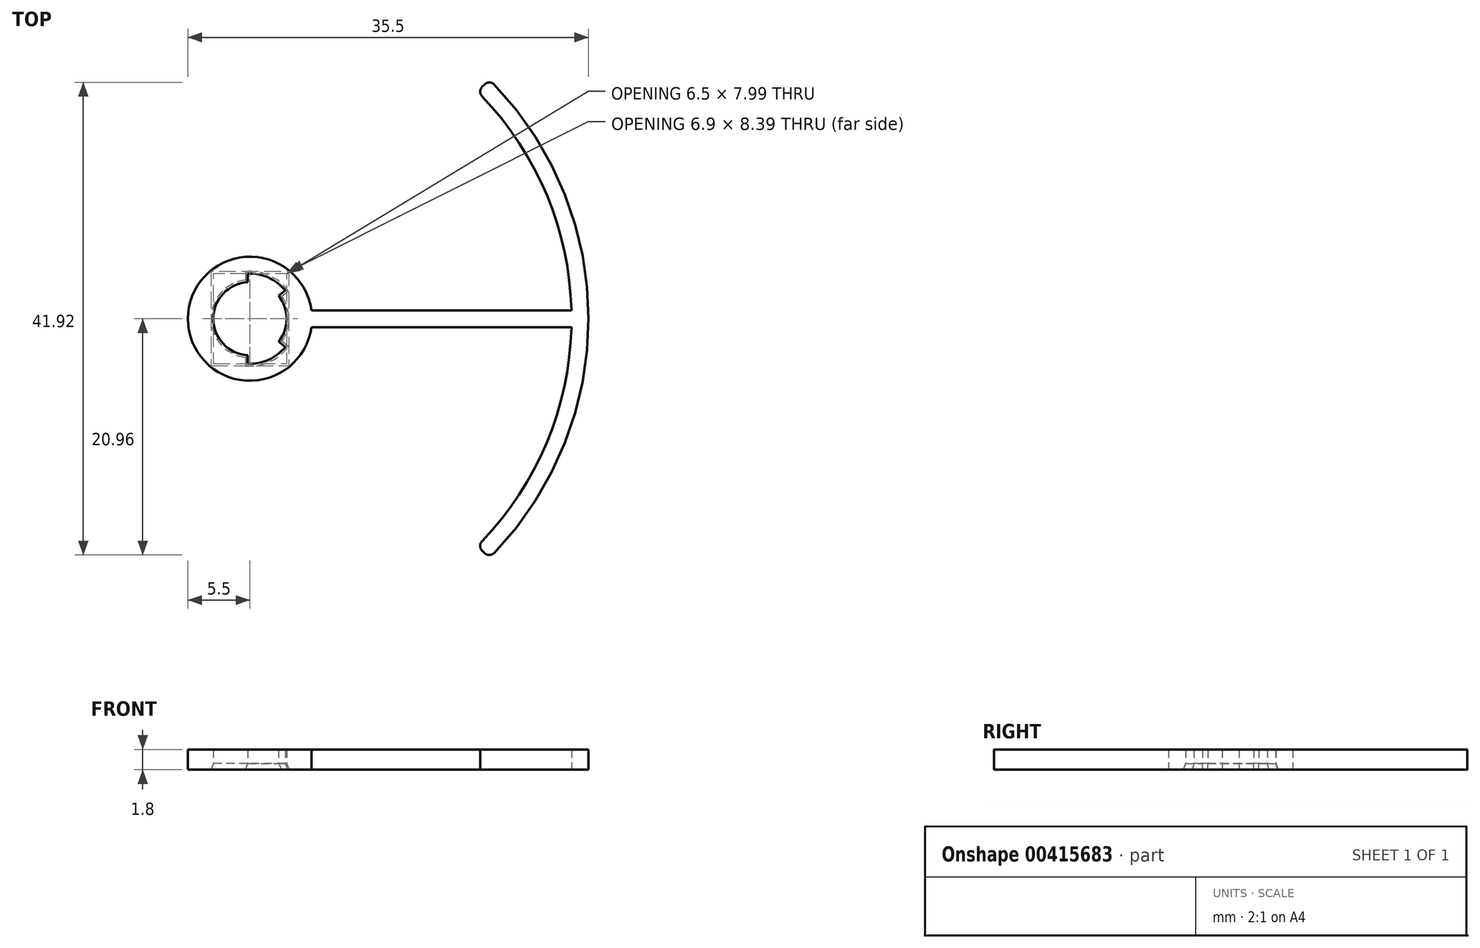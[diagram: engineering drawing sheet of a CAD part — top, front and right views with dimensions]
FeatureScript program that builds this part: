
annotation { "Feature Type Name" : "Feature", "Feature Type Description" : "" }
export const myFeature = defineFeature(function(context is Context, id is Id, definition is map)
    precondition{}
    {
        {
            var Q0;
            Q0=qCreatedBy(makeId("Top.planeOp"),FACE);
            var sketch = newSketch(context, id + "F0", { "sketchPlane" : qUnion([Q0])});
            skCircle(sketch, "E0", {"center": v(0, 0) * mm, "radius": 4 * mm});
            skCircle(sketch, "E1", {"center": v(0, 0) * mm, "radius": 3.25 * mm});
            skCircle(sketch, "E2", {"center": v(0, 0) * mm, "radius": 5.5 * mm});
            skLineSegment(sketch, "E3", {"start": v(-0.2, 4) * mm, "end": v(-0.2, -4) * mm});
            skLineSegment(sketch, "E4", {"start": v(0, 0) * mm, "end": v(3.12, -2.5) * mm});
            skLineSegment(sketch, "E5", {"start": v(0, 0) * mm, "end": v(3.12, 2.5) * mm});
            skPoint(sketch, "E6", {"position": v(3.12, 0) * mm});
            skLineSegment(sketch, "E7.bottom", {"start": v(5.45, -0.75) * mm, "end": v(30, -0.75) * mm});
            skLineSegment(sketch, "E7.top", {"start": v(5.45, 0.75) * mm, "end": v(30, 0.75) * mm});
            skLineSegment(sketch, "E7.left", {"start": v(5.45, -0.75) * mm, "end": v(5.45, 0.75) * mm});
            skLineSegment(sketch, "E7.right", {"start": v(30, -0.75) * mm, "end": v(30, 0.75) * mm});
            skPoint(sketch, "E7.middle", {"position": v(17.72, 0) * mm});
            skCircle(sketch, "E8", {"center": v(0, 0) * mm, "radius": 30 * mm});
            skCircle(sketch, "E9", {"center": v(0, 0) * mm, "radius": 28.5 * mm});
            skLineSegment(sketch, "E10", {"start": v(0, 0) * mm, "end": v(21.21, -21.21) * mm});
            skLineSegment(sketch, "E11", {"start": v(0, 0) * mm, "end": v(21.21, 21.21) * mm});
            skSolve(sketch);
        }
        {
            var Q0;
            {var subQ1=sQuery(id+"F0.wireOp",EDGE,"E7.right");Q0=makeQuery(id+"F0.imprint","IMPRINT",FACE,{"disambiguationData":[TD([[makeQuery(id+"F0.imprint","IMPRINT",EDGE,{"derivedFrom":subQ1}),1.0]])]});}
            var Q1;
            {var subQ1=sQuery(id+"F0.wireOp",EDGE,"E7.top");var subQ3=sQuery(id+"F0.wireOp",EDGE,"E9");var subQ4=makeQuery(id+"F0.imprint","INTERSECT",VERTEX,{"derivedFrom":[subQ1,subQ3]});Q1=makeQuery(id+"F0.imprint","IMPRINT",FACE,{"disambiguationData":[TD([[makeQuery(id+"F0.imprint","IMPRINT",EDGE,{"disambiguationData":[TD([[subQ4,-1.0]])],"derivedFrom":subQ3}),-1.0]])]});}
            var Q2;
            {var subQ1=sQuery(id+"F0.wireOp",EDGE,"E7.bottom");var subQ6=sQuery(id+"F0.wireOp",EDGE,"E9");var subQ8=makeQuery(id+"F0.imprint","INTERSECT",VERTEX,{"derivedFrom":[subQ1,subQ6]});Q2=makeQuery(id+"F0.imprint","IMPRINT",FACE,{"disambiguationData":[TD([[makeQuery(id+"F0.imprint","IMPRINT",EDGE,{"disambiguationData":[TD([[subQ8,-1.0]])],"derivedFrom":subQ6}),1.0]])]});}
            var Q3;
            {var subQ1=sQuery(id+"F0.wireOp",EDGE,"E7.bottom");var subQ3=sQuery(id+"F0.wireOp",EDGE,"E9");var subQ4=makeQuery(id+"F0.imprint","INTERSECT",VERTEX,{"derivedFrom":[subQ1,subQ3]});Q3=makeQuery(id+"F0.imprint","IMPRINT",FACE,{"disambiguationData":[TD([[makeQuery(id+"F0.imprint","IMPRINT",EDGE,{"disambiguationData":[TD([[subQ4,1.0]])],"derivedFrom":subQ3}),-1.0]])]});}
            var Q4;
            {var subQ0=sQuery(id+"F0.wireOp",EDGE,"E7.left");Q4=makeQuery(id+"F0.imprint","IMPRINT",FACE,{"disambiguationData":[TD([[makeQuery(id+"F0.imprint","IMPRINT",EDGE,{"derivedFrom":subQ0}),1.0]])]});}
            var Q5;
            {var subQ0=sQuery(id+"F0.wireOp",EDGE,"E4");var subQ1=sQuery(id+"F0.wireOp",EDGE,"E0");var subQ2=makeQuery(id+"F0.imprint","INTERSECT",VERTEX,{"derivedFrom":[subQ1,subQ0]});Q5=makeQuery(id+"F0.imprint","IMPRINT",FACE,{"disambiguationData":[TD([[makeQuery(id+"F0.imprint","IMPRINT",EDGE,{"disambiguationData":[TD([[subQ2,-1.0]])],"derivedFrom":subQ1}),1.0]])]});}
            var Q6;
            {var subQ0=sQuery(id+"F0.wireOp",EDGE,"E3");var subQ1=sQuery(id+"F0.wireOp",EDGE,"E0");var subQ2=makeQuery(id+"F0.imprint","INTERSECT",VERTEX,{"disambiguationData":[OD(0.0)],"derivedFrom":[subQ1,subQ0]});Q6=makeQuery(id+"F0.imprint","IMPRINT",FACE,{"disambiguationData":[TD([[makeQuery(id+"F0.imprint","IMPRINT",EDGE,{"disambiguationData":[TD([[subQ2,-1.0]])],"derivedFrom":subQ1}),1.0]])]});}
            var Q7;
            {var subQ5=sQuery(id+"F0.wireOp",EDGE,"E3");var subQ6=sQuery(id+"F0.wireOp",EDGE,"E0");var subQ7=makeQuery(id+"F0.imprint","INTERSECT",VERTEX,{"disambiguationData":[OD(0.0)],"derivedFrom":[subQ6,subQ5]});Q7=makeQuery(id+"F0.imprint","IMPRINT",FACE,{"disambiguationData":[TD([[makeQuery(id+"F0.imprint","IMPRINT",EDGE,{"disambiguationData":[TD([[subQ7,1.0]])],"derivedFrom":subQ6}),-1.0]])]});}
            var Q8;
            {var subQ0=sQuery(id+"F0.wireOp",EDGE,"E7.left");Q8=makeQuery(id+"F0.imprint","IMPRINT",FACE,{"disambiguationData":[TD([[makeQuery(id+"F0.imprint","IMPRINT",EDGE,{"derivedFrom":subQ0}),-1.0]])]});}
            var Q9;
            {var subQ0=sQuery(id+"F0.wireOp",EDGE,"E7.right");Q9=makeQuery(id+"F0.imprint","IMPRINT",FACE,{"disambiguationData":[TD([[makeQuery(id+"F0.imprint","IMPRINT",EDGE,{"derivedFrom":subQ0}),-1.0]])]});}
            extrude(context, id + "F1", {"entities" : qUnion([Q0, Q1, Q2, Q3, Q4, Q5, Q6, Q7, Q8, Q9]), "depth" : 1.8 * mm});
        }
        {
            var Q0;
            Q0=makeQuery(id+"F1.opExtrude","SWEPT_EDGE",EDGE,{"disambiguationData":[OSD([sQuery(id+"F0.wireOp",EDGE,"E8"),sQuery(id+"F0.wireOp",EDGE,"E10")])]});
            var Q1;
            Q1=makeQuery(id+"F1.opExtrude","SWEPT_EDGE",EDGE,{"disambiguationData":[OSD([sQuery(id+"F0.wireOp",EDGE,"E9"),sQuery(id+"F0.wireOp",EDGE,"E10")])]});
            var Q2;
            Q2=makeQuery(id+"F1.opExtrude","SWEPT_EDGE",EDGE,{"disambiguationData":[OSD([sQuery(id+"F0.wireOp",EDGE,"E8"),sQuery(id+"F0.wireOp",EDGE,"E11")])]});
            var Q3;
            Q3=makeQuery(id+"F1.opExtrude","SWEPT_EDGE",EDGE,{"disambiguationData":[OSD([sQuery(id+"F0.wireOp",EDGE,"E9"),sQuery(id+"F0.wireOp",EDGE,"E11")])]});
            fillet(context, id + "F2", {"entities" : qUnion([Q0, Q1, Q2, Q3]), "radius" : 0.6 * mm, "tangentPropagation" : true, "allowEdgeOverflow" : false});
        }
        {
            var Q0;
            {var subQ0=sQuery(id+"F0.wireOp",EDGE,"E3");var subQ1=sQuery(id+"F0.wireOp",EDGE,"E1");Q0=makeQuery(id+"F1.opExtrude","CAP_EDGE",EDGE,{"disambiguationData":[OSD([subQ1]),TDD([makeQuery(id+"F0.imprint","IMPRINT",EDGE,{"disambiguationData":[TD([[makeQuery(id+"F0.imprint","INTERSECT",VERTEX,{"disambiguationData":[OD(0.0)],"derivedFrom":[subQ1,subQ0]}),-1.0]])],"derivedFrom":subQ1})])],"isStart":true});}
            var Q1;
            {var subQ0=sQuery(id+"F0.wireOp",EDGE,"E3");Q1=makeQuery(id+"F1.opExtrude","CAP_EDGE",EDGE,{"disambiguationData":[OSD([subQ0]),TDD([makeQuery(id+"F0.imprint","IMPRINT",EDGE,{"disambiguationData":[TD([[makeQuery(id+"F0.imprint","INTERSECT",VERTEX,{"disambiguationData":[OD(0.0)],"derivedFrom":[sQuery(id+"F0.wireOp",EDGE,"E0"),subQ0]}),-1.0]])],"derivedFrom":subQ0})])],"isStart":true});}
            var Q2;
            {var subQ0=sQuery(id+"F0.wireOp",EDGE,"E0");Q2=makeQuery(id+"F1.opExtrude","CAP_EDGE",EDGE,{"disambiguationData":[OSD([subQ0]),TDD([makeQuery(id+"F0.imprint","IMPRINT",EDGE,{"disambiguationData":[TD([[makeQuery(id+"F0.imprint","INTERSECT",VERTEX,{"derivedFrom":[subQ0,sQuery(id+"F0.wireOp",EDGE,"E5")]}),-1.0]])],"derivedFrom":subQ0}),makeQuery(id+"F0.imprint","IMPRINT",EDGE,{"disambiguationData":[TD([[makeQuery(id+"F0.imprint","INTERSECT",VERTEX,{"disambiguationData":[OD(0.0)],"derivedFrom":[subQ0,sQuery(id+"F0.wireOp",EDGE,"E3")]}),1.0]])],"derivedFrom":subQ0})])],"isStart":true});}
            var Q3;
            {var subQ0=sQuery(id+"F0.wireOp",EDGE,"E1");Q3=makeQuery(id+"F1.opExtrude","CAP_EDGE",EDGE,{"disambiguationData":[OSD([subQ0]),TDD([makeQuery(id+"F0.imprint","IMPRINT",EDGE,{"disambiguationData":[TD([[makeQuery(id+"F0.imprint","INTERSECT",VERTEX,{"derivedFrom":[subQ0,sQuery(id+"F0.wireOp",EDGE,"E5")]}),1.0]])],"derivedFrom":subQ0})])],"isStart":true});}
            var Q4;
            Q4=makeQuery(id+"F1.opExtrude","CAP_EDGE",EDGE,{"disambiguationData":[OSD([sQuery(id+"F0.wireOp",EDGE,"E5")])],"isStart":true});
            var Q5;
            Q5=makeQuery(id+"F1.opExtrude","CAP_EDGE",EDGE,{"disambiguationData":[OSD([sQuery(id+"F0.wireOp",EDGE,"E4")])],"isStart":true});
            var Q6;
            {var subQ0=sQuery(id+"F0.wireOp",EDGE,"E0");Q6=makeQuery(id+"F1.opExtrude","CAP_EDGE",EDGE,{"disambiguationData":[OSD([subQ0]),TDD([makeQuery(id+"F0.imprint","IMPRINT",EDGE,{"disambiguationData":[TD([[makeQuery(id+"F0.imprint","INTERSECT",VERTEX,{"disambiguationData":[OD(1.0)],"derivedFrom":[subQ0,sQuery(id+"F0.wireOp",EDGE,"E3")]}),-1.0]])],"derivedFrom":subQ0}),makeQuery(id+"F0.imprint","IMPRINT",EDGE,{"disambiguationData":[TD([[makeQuery(id+"F0.imprint","INTERSECT",VERTEX,{"derivedFrom":[subQ0,sQuery(id+"F0.wireOp",EDGE,"E4")]}),1.0]])],"derivedFrom":subQ0})])],"isStart":true});}
            var Q7;
            {var subQ0=sQuery(id+"F0.wireOp",EDGE,"E3");Q7=makeQuery(id+"F1.opExtrude","CAP_EDGE",EDGE,{"disambiguationData":[OSD([subQ0]),TDD([makeQuery(id+"F0.imprint","IMPRINT",EDGE,{"disambiguationData":[TD([[makeQuery(id+"F0.imprint","INTERSECT",VERTEX,{"disambiguationData":[OD(1.0)],"derivedFrom":[sQuery(id+"F0.wireOp",EDGE,"E0"),subQ0]}),1.0]])],"derivedFrom":subQ0})])],"isStart":true});}
            chamfer(context, id + "F3", {"entities" : qUnion([Q0, Q1, Q2, Q3, Q4, Q5, Q6, Q7]), "chamferType" : ChamferType.OFFSET_ANGLE, "width" : 0.2 * mm, "oppositeDirection" : false, "angle" : 70 * degree, "tangentPropagation" : true});
        }
    });
